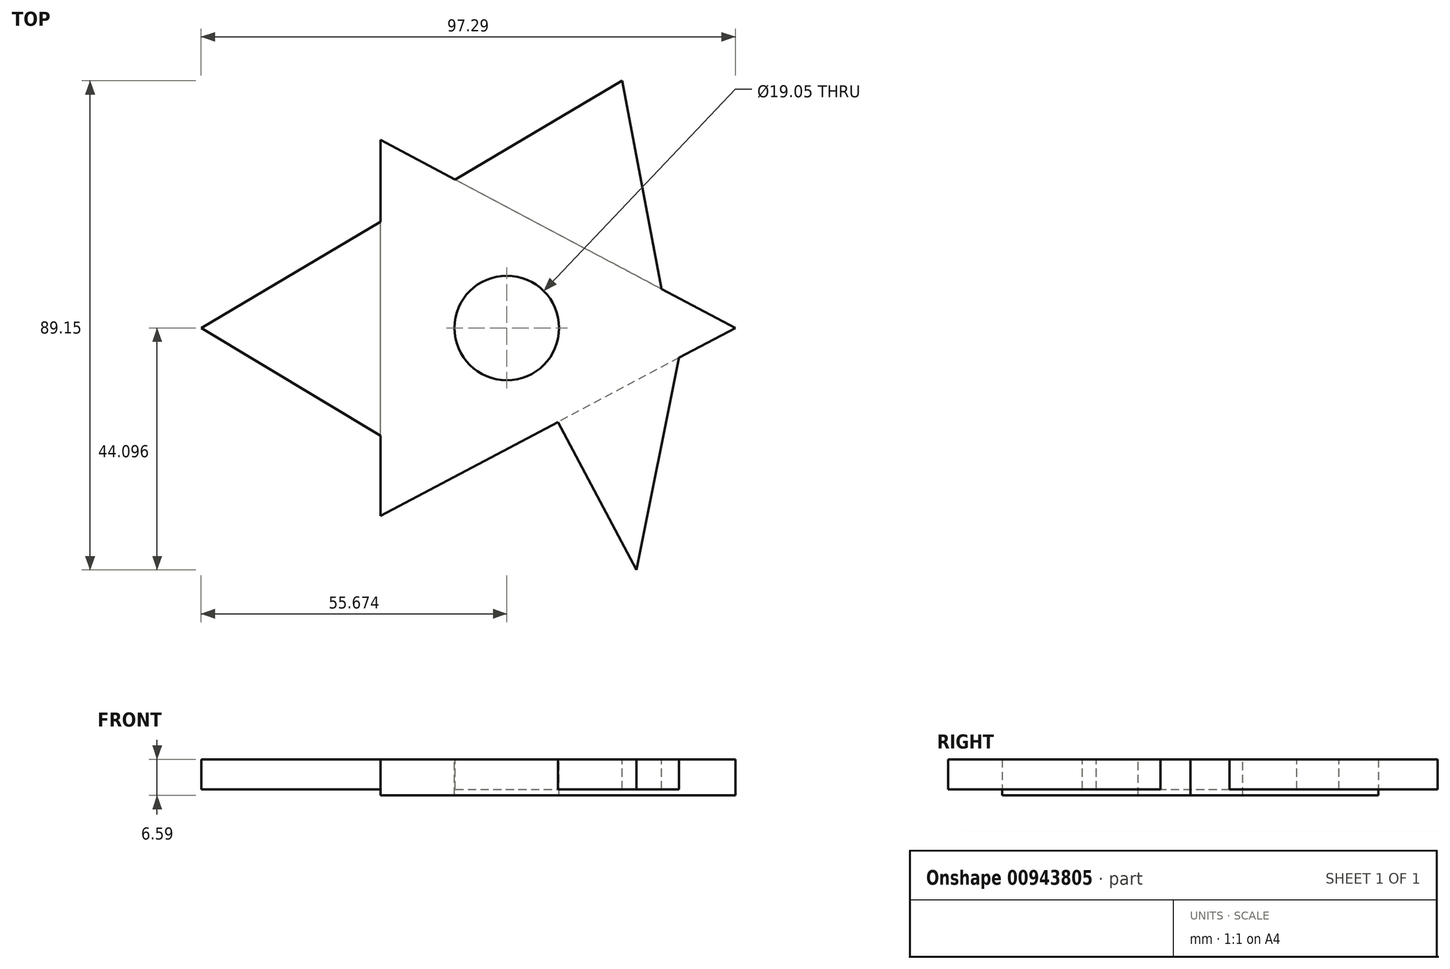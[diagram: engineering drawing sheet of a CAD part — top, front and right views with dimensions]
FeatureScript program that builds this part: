
annotation { "Feature Type Name" : "Feature", "Feature Type Description" : "" }
export const myFeature = defineFeature(function(context is Context, id is Id, definition is map)
    precondition{}
    {
        {
            var Q0;
            Q0=qCreatedBy(makeId("Top.planeOp"),FACE);
            var sketch = newSketch(context, id + "F0", { "sketchPlane" : qUnion([Q0])});
            skLineSegment(sketch, "E0", {"start": v(-64.6, 0) * mm, "end": v(-64.6, 68.51) * mm});
            skLineSegment(sketch, "E1", {"start": v(-64.6, 68.51) * mm, "end": v(0, 34.26) * mm});
            skPoint(sketch, "E1.endSnap0", {"position": v(-64.6, 34.26) * mm});
            skLineSegment(sketch, "E2", {"start": v(0, 34.26) * mm, "end": v(-64.6, 0) * mm});
            skSolve(sketch);
        }
        {
            var Q0;
            Q0=makeQuery(id+"F0.imprint","IMPRINT",FACE,{"disambiguationData":[TD([[makeQuery(id+"F0.imprint","IMPRINT",EDGE,{"derivedFrom":sQuery(id+"F0.wireOp",EDGE,"E0")}),-1.0]])]});
            extrude(context, id + "F1", {"entities" : qUnion([Q0]), "depth" : 6.6 * mm, "offsetDistance" : 25.4 * mm});
        }
        {
            var Q0;
            Q0=makeQuery(id+"F1.opExtrude","CAP_FACE",FACE,{"disambiguationData":[OSD([sQuery(id+"F0.wireOp",EDGE,"E0"),sQuery(id+"F0.wireOp",EDGE,"E1"),sQuery(id+"F0.wireOp",EDGE,"E2")])],"isStart":false});
            var sketch = newSketch(context, id + "F2", { "sketchPlane" : qUnion([Q0])});
            skPoint(sketch, "E3", {"position": v(-41.62, 34.26) * mm});
            skSolve(sketch);
        }
        {
            var Q0;
            Q0=sQuery(id+"F2.wireOp",VERTEX,"E3");
            var Q1;
            Q1=makeQuery(id+"F1.opExtrude","SWEPT_BODY",BODY,{"disambiguationData":[OSD([sQuery(id+"F0.wireOp",EDGE,"E0"),sQuery(id+"F0.wireOp",EDGE,"E1"),sQuery(id+"F0.wireOp",EDGE,"E2")])]});
            hole(context, id + "F3", {"style" : HoleStyle.SIMPLE, "endStyle" : HoleEndStyle.THROUGH, "holeDiameter" : 19.05 * mm, "majorDiameter" : 6.35 * mm, "isTappedThrough" : true, "tappedDepth" : 12.7 * mm, "tapClearance" : 3, "locations" : qUnion([Q0]), "scope" : qUnion([Q1])});
        }
        {
            var Q0;
            Q0=makeQuery(id+"F1.opExtrude","CAP_FACE",FACE,{"disambiguationData":[OSD([sQuery(id+"F0.wireOp",EDGE,"E0"),sQuery(id+"F0.wireOp",EDGE,"E1"),sQuery(id+"F0.wireOp",EDGE,"E2")])],"isStart":false});
            var sketch = newSketch(context, id + "F4", { "sketchPlane" : qUnion([Q0])});
            skLineSegment(sketch, "E4", {"start": v(-64.6, 14.6) * mm, "end": v(-64.6, 34.26) * mm});
            skLineSegment(sketch, "E5", {"start": v(-64.6, 34.26) * mm, "end": v(-64.6, 53.63) * mm});
            skLineSegment(sketch, "E6", {"start": v(-64.6, 53.63) * mm, "end": v(-97.29, 34.26) * mm});
            skLineSegment(sketch, "E7", {"start": v(-97.29, 34.26) * mm, "end": v(-64.6, 14.6) * mm});
            skLineSegment(sketch, "E8", {"start": v(-32.3, 51.38) * mm, "end": v(-51, 61.3) * mm});
            skLineSegment(sketch, "E9", {"start": v(-51, 61.3) * mm, "end": v(-20.63, 79.3) * mm});
            skLineSegment(sketch, "E10", {"start": v(-20.63, 79.3) * mm, "end": v(-13.45, 41.39) * mm});
            skLineSegment(sketch, "E11", {"start": v(-32.3, 17.13) * mm, "end": v(-53.03, 6.13) * mm});
            skLineSegment(sketch, "E12", {"start": v(-53.03, 6.13) * mm, "end": v(-32.3, 17.13) * mm});
            skLineSegment(sketch, "E13", {"start": v(-32.3, 17.13) * mm, "end": v(-18, -9.84) * mm});
            skLineSegment(sketch, "E14", {"start": v(-18, -9.84) * mm, "end": v(-53.03, 6.13) * mm});
            skLineSegment(sketch, "E15", {"start": v(-10.23, 28.83) * mm, "end": v(-18, -9.84) * mm});
            skSolve(sketch);
        }
        {
            var Q0;
            Q0=makeQuery(id+"F4.imprint","IMPRINT",FACE,{"disambiguationData":[TD([[makeQuery(id+"F4.imprint","IMPRINT",EDGE,{"derivedFrom":sQuery(id+"F4.wireOp",EDGE,"E4")}),1.0]])]});
            var Q1;
            Q1=makeQuery(id+"F4.imprint","IMPRINT",FACE,{"disambiguationData":[TD([[makeQuery(id+"F4.imprint","IMPRINT",EDGE,{"derivedFrom":sQuery(id+"F4.wireOp",EDGE,"E12")}),1.0]])]});
            var Q2;
            {var subQ0=sQuery(id+"F4.wireOp",EDGE,"E13");Q2=makeQuery(id+"F4.imprint","IMPRINT",FACE,{"disambiguationData":[TD([[makeQuery(id+"F4.imprint","IMPRINT",EDGE,{"derivedFrom":subQ0}),1.0]])]});}
            var Q3;
            {var subQ0=sQuery(id+"F4.wireOp",EDGE,"E8");Q3=makeQuery(id+"F4.imprint","IMPRINT",FACE,{"disambiguationData":[TD([[makeQuery(id+"F4.imprint","IMPRINT",EDGE,{"derivedFrom":subQ0}),1.0]])]});}
            extrude(context, id + "F5", {"entities" : qUnion([Q0, Q1, Q2, Q3]), "operationType" : NewBodyOperationType.ADD, "oppositeDirection" : true, "depth" : 5.5 * mm, "offsetDistance" : 25.4 * mm});
        }
    });
